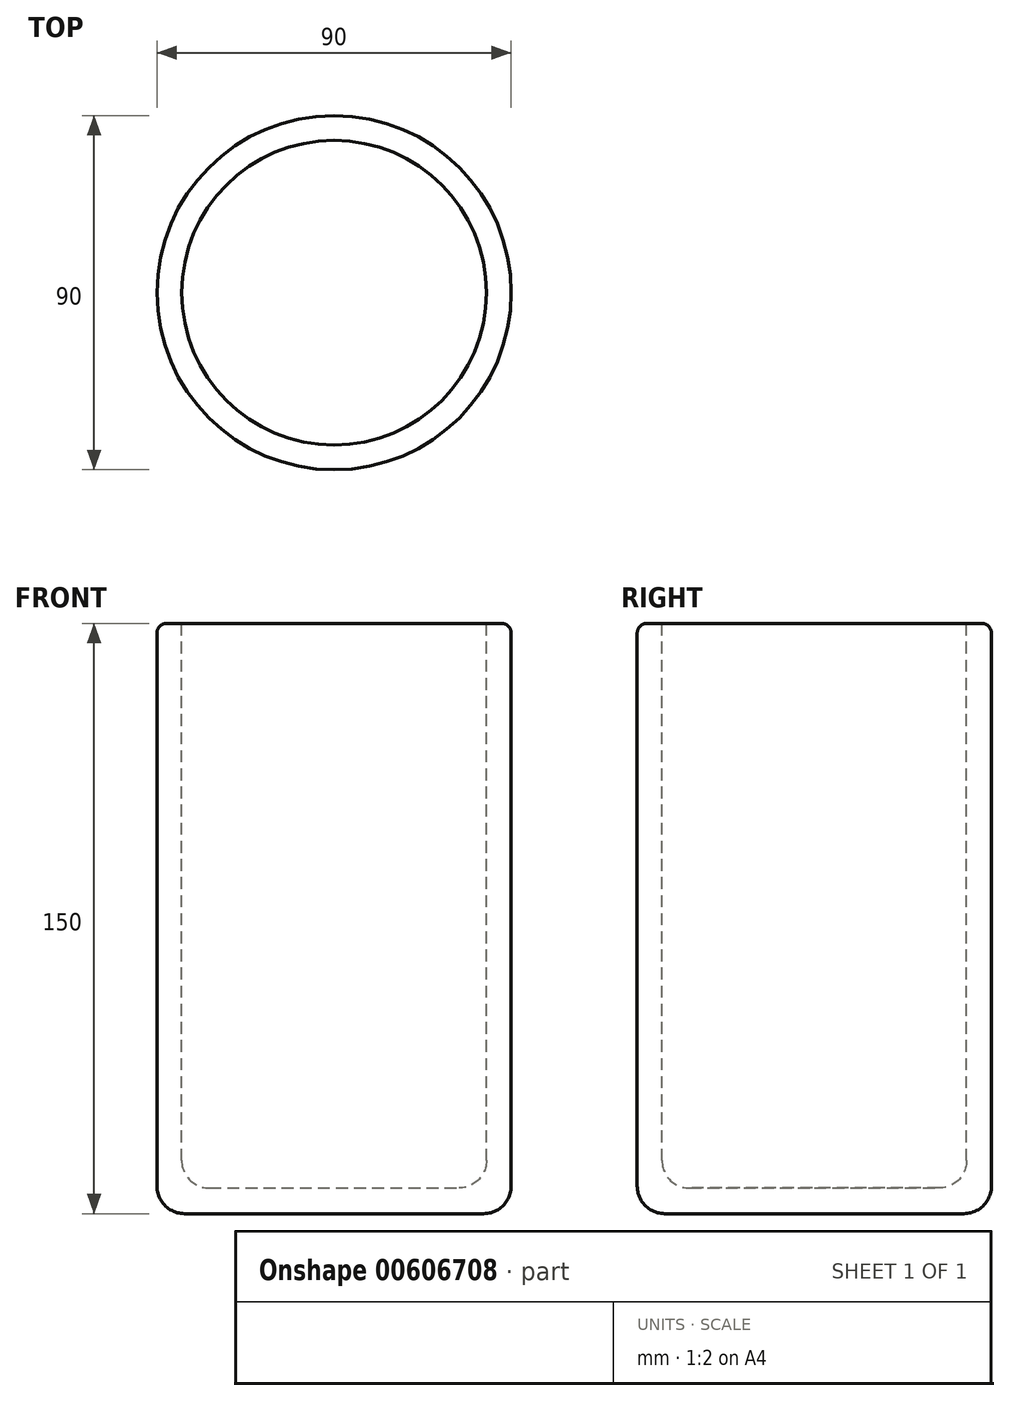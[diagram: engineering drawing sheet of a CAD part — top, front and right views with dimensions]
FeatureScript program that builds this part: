
annotation { "Feature Type Name" : "Feature", "Feature Type Description" : "" }
export const myFeature = defineFeature(function(context is Context, id is Id, definition is map)
    precondition{}
    {
        {
            var Q0;
            Q0=qCreatedBy(makeId("Top.planeOp"),FACE);
            var sketch = newSketch(context, id + "F0", { "sketchPlane" : qUnion([Q0])});
            skCircle(sketch, "E0", {"center": v(0, 0) * mm, "radius": 45 * mm});
            skSolve(sketch);
        }
        {
            var Q0;
            Q0=makeQuery(id+"F0.imprint","IMPRINT",FACE,{"disambiguationData":[TD([[makeQuery(id+"F0.imprint","IMPRINT",EDGE,{"derivedFrom":sQuery(id+"F0.wireOp",EDGE,"E0")}),1.0]])]});
            extrude(context, id + "F1", {"entities" : qUnion([Q0]), "depth" : 150 * mm, "offsetDistance" : 25 * mm});
        }
        {
            var Q0;
            Q0=makeQuery(id+"F1.opExtrude","CAP_FACE",FACE,{"disambiguationData":[OSD([sQuery(id+"F0.wireOp",EDGE,"E0")])],"isStart":false});
            var sketch = newSketch(context, id + "F2", { "sketchPlane" : qUnion([Q0])});
            skCircle(sketch, "E1.0", {"center": v(0, 0) * mm, "radius": 38.7 * mm});
            skSolve(sketch);
        }
        {
            var Q0;
            Q0=qCreatedBy(makeId("Right.planeOp"),FACE);
            var sketch = newSketch(context, id + "F3", { "sketchPlane" : qUnion([Q0])});
            skLineSegment(sketch, "E2", {"start": v(0, 0) * mm, "end": v(0, 6.5) * mm});
            skSolve(sketch);
        }
        {
            var Q0;
            Q0=makeQuery(id+"F2.imprint","IMPRINT",FACE,{"disambiguationData":[TD([[makeQuery(id+"F2.imprint","IMPRINT",EDGE,{"derivedFrom":sQuery(id+"F2.wireOp",EDGE,"E1.0")}),1.0]])]});
            var Q1;
            Q1=sQuery(id+"F3.wireOp",VERTEX,"E2.end");
            extrude(context, id + "F4", {"entities" : qUnion([Q0]), "operationType" : NewBodyOperationType.REMOVE, "endBound" : BoundingType.UP_TO_VERTEX, "oppositeDirection" : true, "depth" : mm, "endBoundEntityVertex" : qUnion([Q1]), "offsetDistance" : 25 * mm});
        }
        {
            var Q0;
            Q0=makeQuery(id+"F1.opExtrude","CAP_EDGE",EDGE,{"disambiguationData":[OSD([sQuery(id+"F0.wireOp",EDGE,"E0")])],"isStart":false});
            var Q1;
            Q1=makeQuery(id+"F4.boolean.opBoolean","COPY",EDGE,{"derivedFrom":makeQuery(id+"F4.opExtrude","CAP_EDGE",EDGE,{"disambiguationData":[OSD([sQuery(id+"F2.wireOp",EDGE,"E1.0")])],"isStart":true})});
            fillet(context, id + "F5", {"entities" : qUnion([Q0, Q1]), "radius" : 2.5 * mm, "tangentPropagation" : true, "allowEdgeOverflow" : false});
        }
        {
            var Q0;
            Q0=makeQuery(id+"F4.boolean.opBoolean","COPY",EDGE,{"derivedFrom":makeQuery(id+"F4.opExtrude","CAP_EDGE",EDGE,{"disambiguationData":[OSD([sQuery(id+"F2.wireOp",EDGE,"E1.0")])],"isStart":false})});
            var Q1;
            Q1=makeQuery(id+"F1.opExtrude","CAP_EDGE",EDGE,{"disambiguationData":[OSD([sQuery(id+"F0.wireOp",EDGE,"E0")])],"isStart":true});
            fillet(context, id + "F6", {"entities" : qUnion([Q0, Q1]), "radius" : 7 * mm, "tangentPropagation" : true, "allowEdgeOverflow" : false});
        }
    });
